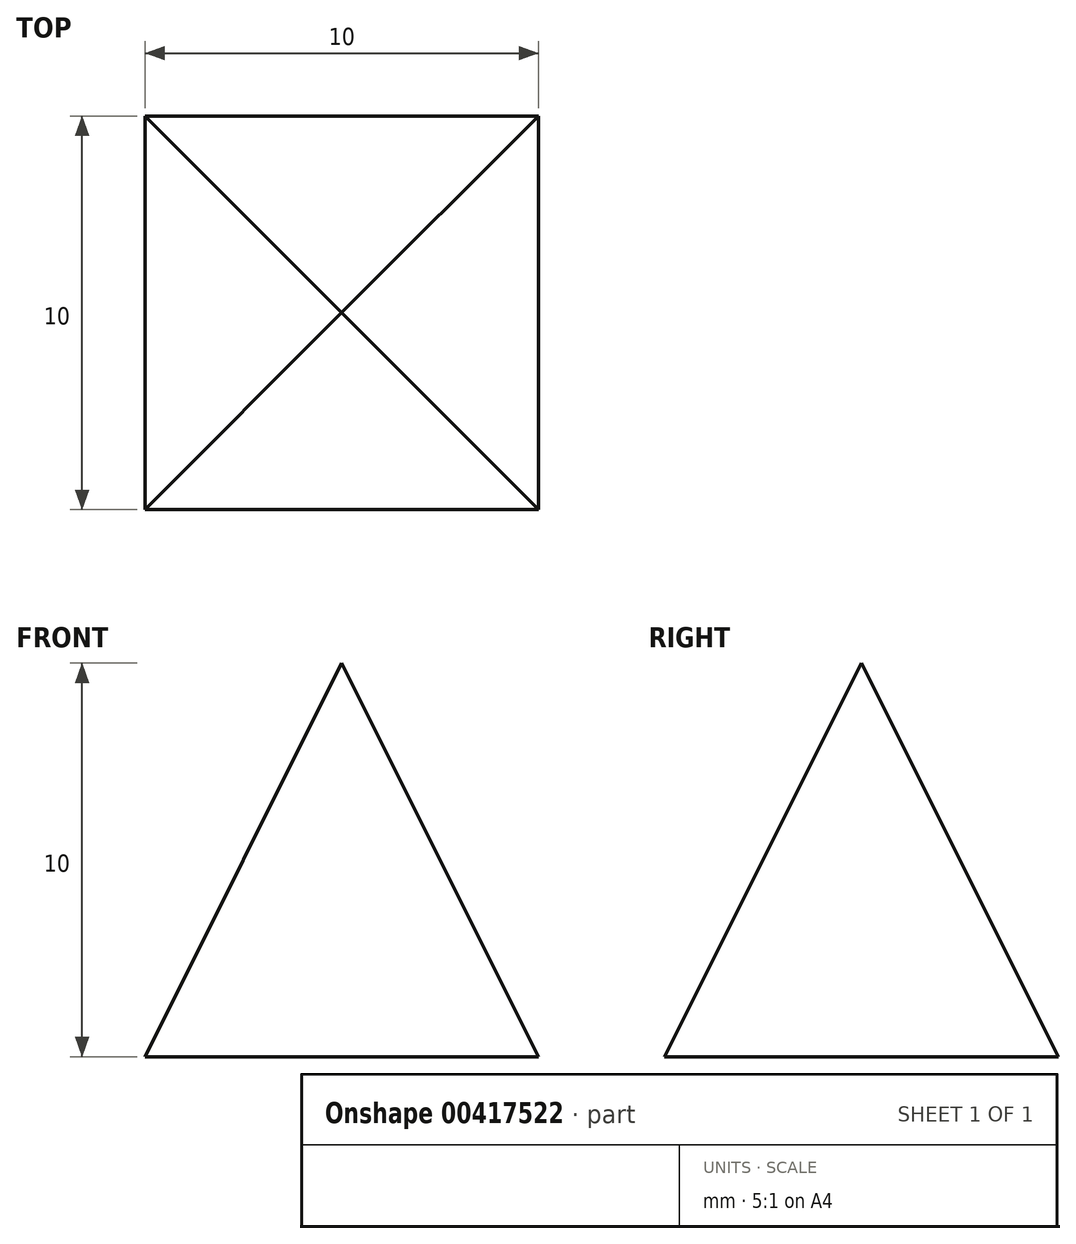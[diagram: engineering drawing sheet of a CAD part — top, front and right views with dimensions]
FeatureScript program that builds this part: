
annotation { "Feature Type Name" : "Feature", "Feature Type Description" : "" }
export const myFeature = defineFeature(function(context is Context, id is Id, definition is map)
    precondition{}
    {
        {
            var Q0;
            Q0=qCreatedBy(makeId("Top.planeOp"),FACE);
            cPlane(context, id + "F0", {"entities" : qUnion([Q0]), "cplaneType" : CPlaneType.OFFSET, "offset" : 10 * mm, "oppositeDirection" : true, "width" : 150 * mm, "height" : 150 * mm});
        }
        {
            var Q0;
            Q0=qCreatedBy(id+"F0.planeOp",FACE);
            var sketch = newSketch(context, id + "F1", { "sketchPlane" : qUnion([Q0])});
            skLineSegment(sketch, "E0.bottom", {"start": v(5, -5) * mm, "end": v(-5, -5) * mm});
            skLineSegment(sketch, "E0.top", {"start": v(5, 5) * mm, "end": v(-5, 5) * mm});
            skLineSegment(sketch, "E0.left", {"start": v(5, -5) * mm, "end": v(5, 5) * mm});
            skLineSegment(sketch, "E0.right", {"start": v(-5, -5) * mm, "end": v(-5, 5) * mm});
            skPoint(sketch, "E0.middle", {"position": v(0, 0) * mm});
            skSolve(sketch);
        }
        {
            var Q0;
            Q0=makeQuery(id+"F1.imprint","IMPRINT",FACE,{"disambiguationData":[TD([[makeQuery(id+"F1.imprint","IMPRINT",EDGE,{"derivedFrom":sQuery(id+"F1.wireOp",EDGE,"E0.bottom")}),-1.0]])]});
            var Q1;
            Q1=qCreatedBy(makeId("Origin.pointOp"),VERTEX);
            loft(context, id + "F2", {"sheetProfilesArray" : [{ "sheetProfileEntities" : qUnion([Q0]) }, { "sheetProfileEntities" : qUnion([Q1]) }]});
        }
    });
